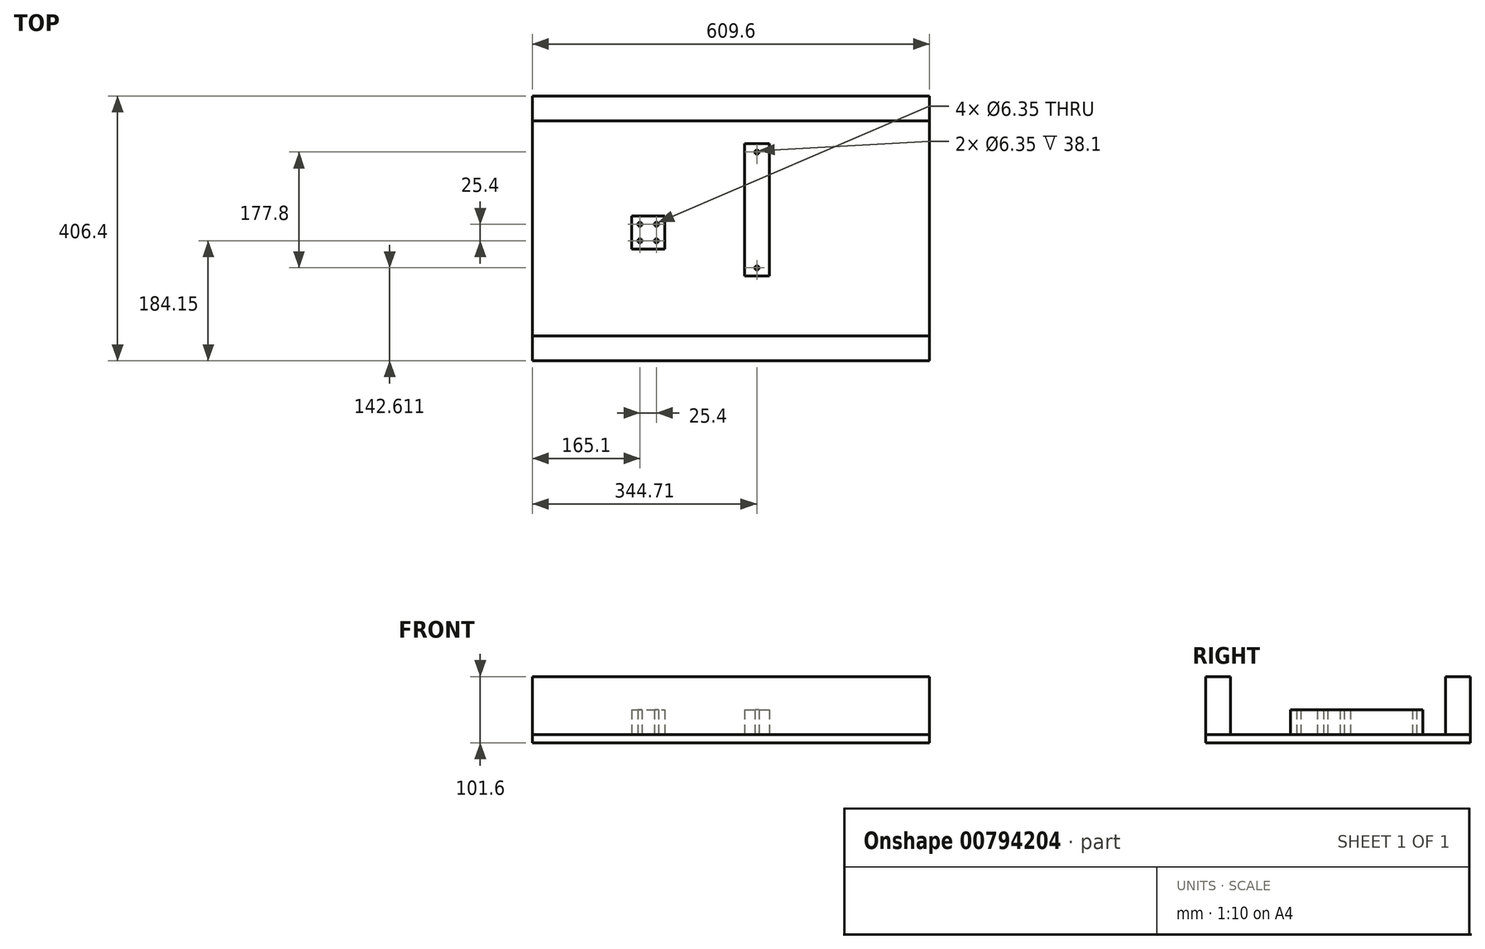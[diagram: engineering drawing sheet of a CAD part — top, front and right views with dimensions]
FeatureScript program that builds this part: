
annotation { "Feature Type Name" : "Feature", "Feature Type Description" : "" }
export const myFeature = defineFeature(function(context is Context, id is Id, definition is map)
    precondition{}
    {
        {
            var Q0;
            Q0=qCreatedBy(makeId("Top.planeOp"),FACE);
            var sketch = newSketch(context, id + "F0", { "sketchPlane" : qUnion([Q0])});
            skLineSegment(sketch, "E0.bottom", {"start": v(304.8, -203.2) * mm, "end": v(-304.8, -203.2) * mm});
            skLineSegment(sketch, "E0.top", {"start": v(304.8, 203.2) * mm, "end": v(-304.8, 203.2) * mm});
            skLineSegment(sketch, "E0.left", {"start": v(304.8, -203.2) * mm, "end": v(304.8, 203.2) * mm});
            skLineSegment(sketch, "E0.right", {"start": v(-304.8, -203.2) * mm, "end": v(-304.8, 203.2) * mm});
            skPoint(sketch, "E0.middle", {"position": v(0, 0) * mm});
            skSolve(sketch);
        }
        {
            var Q0;
            Q0=makeQuery(id+"F0.imprint","IMPRINT",FACE,{"disambiguationData":[TD([[makeQuery(id+"F0.imprint","IMPRINT",EDGE,{"derivedFrom":sQuery(id+"F0.wireOp",EDGE,"E0.bottom")}),-1.0]])]});
            extrude(context, id + "F1", {"entities" : qUnion([Q0]), "depth" : 12.7 * mm, "offsetDistance" : 25.4 * mm});
        }
        {
            var Q0;
            Q0=makeQuery(id+"F1.opExtrude","CAP_FACE",FACE,{"disambiguationData":[OSD([sQuery(id+"F0.wireOp",EDGE,"E0.bottom"),sQuery(id+"F0.wireOp",EDGE,"E0.top"),sQuery(id+"F0.wireOp",EDGE,"E0.left"),sQuery(id+"F0.wireOp",EDGE,"E0.right")])],"isStart":false});
            var sketch = newSketch(context, id + "F2", { "sketchPlane" : qUnion([Q0])});
            skLineSegment(sketch, "E1.bottom", {"start": v(-304.8, -203.2) * mm, "end": v(304.8, -203.2) * mm});
            skLineSegment(sketch, "E1.top", {"start": v(-304.8, -165.1) * mm, "end": v(304.8, -165.1) * mm});
            skLineSegment(sketch, "E1.left", {"start": v(-304.8, -203.2) * mm, "end": v(-304.8, -165.1) * mm});
            skLineSegment(sketch, "E1.right", {"start": v(304.8, -203.2) * mm, "end": v(304.8, -165.1) * mm});
            skLineSegment(sketch, "E2.bottom", {"start": v(-304.8, 203.2) * mm, "end": v(304.8, 203.2) * mm});
            skLineSegment(sketch, "E2.top", {"start": v(-304.8, 165.1) * mm, "end": v(304.8, 165.1) * mm});
            skLineSegment(sketch, "E2.left", {"start": v(-304.8, 203.2) * mm, "end": v(-304.8, 165.1) * mm});
            skLineSegment(sketch, "E2.right", {"start": v(304.8, 203.2) * mm, "end": v(304.8, 165.1) * mm});
            skSolve(sketch);
        }
        {
            var Q0;
            Q0=makeQuery(id+"F2.imprint","IMPRINT",FACE,{"disambiguationData":[TD([[makeQuery(id+"F2.imprint","IMPRINT",EDGE,{"derivedFrom":sQuery(id+"F2.wireOp",EDGE,"E2.bottom")}),1.0]])]});
            var Q1;
            Q1=makeQuery(id+"F2.imprint","IMPRINT",FACE,{"disambiguationData":[TD([[makeQuery(id+"F2.imprint","IMPRINT",EDGE,{"derivedFrom":sQuery(id+"F2.wireOp",EDGE,"E1.bottom")}),-1.0]])]});
            extrude(context, id + "F3", {"entities" : qUnion([Q0, Q1]), "depth" : 88.9 * mm, "offsetDistance" : 25.4 * mm});
        }
        {
            var Q0;
            Q0=makeQuery(id+"F1.opExtrude","CAP_FACE",FACE,{"disambiguationData":[OSD([sQuery(id+"F0.wireOp",EDGE,"E0.bottom"),sQuery(id+"F0.wireOp",EDGE,"E0.top"),sQuery(id+"F0.wireOp",EDGE,"E0.left"),sQuery(id+"F0.wireOp",EDGE,"E0.right")])],"isStart":false});
            var sketch = newSketch(context, id + "F4", { "sketchPlane" : qUnion([Q0])});
            skLineSegment(sketch, "E3.bottom", {"start": v(-152.4, 19.05) * mm, "end": v(-101.6, 19.05) * mm});
            skLineSegment(sketch, "E3.top", {"start": v(-152.4, -31.75) * mm, "end": v(-101.6, -31.75) * mm});
            skLineSegment(sketch, "E3.left", {"start": v(-152.4, 19.05) * mm, "end": v(-152.4, -31.75) * mm});
            skLineSegment(sketch, "E3.right", {"start": v(-101.6, 19.05) * mm, "end": v(-101.6, -31.75) * mm});
            skCircle(sketch, "E4", {"center": v(-139.7, 6.35) * mm, "radius": 3.18 * mm});
            skCircle(sketch, "E5.0.1.0", {"center": v(-139.7, -19.05) * mm, "radius": 3.18 * mm});
            skCircle(sketch, "E5.1.0.0", {"center": v(-114.3, 6.35) * mm, "radius": 3.18 * mm});
            skCircle(sketch, "E5.1.1.0", {"center": v(-114.3, -19.05) * mm, "radius": 3.18 * mm});
            skLineSegment(sketch, "E5.direction1", {"start": v(-139.7, 6.35) * mm, "end": v(-114.3, 6.35) * mm, "construction": true});
            skLineSegment(sketch, "E5.direction2", {"start": v(-139.7, 6.35) * mm, "end": v(-139.7, -19.05) * mm, "construction": true});
            skSolve(sketch);
        }
        {
            var Q0;
            Q0=makeQuery(id+"F4.imprint","IMPRINT",FACE,{"disambiguationData":[TD([[makeQuery(id+"F4.imprint","IMPRINT",EDGE,{"derivedFrom":sQuery(id+"F4.wireOp",EDGE,"E3.bottom")}),-1.0]])]});
            extrude(context, id + "F5", {"entities" : qUnion([Q0]), "depth" : 38.1 * mm, "offsetDistance" : 25.4 * mm});
        }
        {
            var Q0;
            Q0=makeQuery(id+"F1.opExtrude","CAP_FACE",FACE,{"disambiguationData":[OSD([sQuery(id+"F0.wireOp",EDGE,"E0.bottom"),sQuery(id+"F0.wireOp",EDGE,"E0.top"),sQuery(id+"F0.wireOp",EDGE,"E0.left"),sQuery(id+"F0.wireOp",EDGE,"E0.right")])],"isStart":false});
            var sketch = newSketch(context, id + "F6", { "sketchPlane" : qUnion([Q0])});
            skLineSegment(sketch, "E6.bottom", {"start": v(20.86, 129.91) * mm, "end": v(58.96, 129.91) * mm});
            skLineSegment(sketch, "E6.top", {"start": v(20.86, -73.29) * mm, "end": v(58.96, -73.29) * mm});
            skLineSegment(sketch, "E6.left", {"start": v(20.86, 129.91) * mm, "end": v(20.86, -73.29) * mm});
            skLineSegment(sketch, "E6.right", {"start": v(58.96, 129.91) * mm, "end": v(58.96, -73.29) * mm});
            skCircle(sketch, "E7", {"center": v(39.91, 117.21) * mm, "radius": 3.18 * mm});
            skPoint(sketch, "E7.centerSnap0", {"position": v(39.91, 129.91) * mm});
            skCircle(sketch, "E8.0.1.0", {"center": v(39.91, -60.59) * mm, "radius": 3.18 * mm});
            skLineSegment(sketch, "E8.direction1", {"start": v(39.91, 117.21) * mm, "end": v(65.31, 117.21) * mm, "construction": true});
            skLineSegment(sketch, "E8.direction2", {"start": v(39.91, 117.21) * mm, "end": v(39.91, -60.59) * mm, "construction": true});
            skSolve(sketch);
        }
        {
            var Q0;
            Q0=makeQuery(id+"F6.imprint","IMPRINT",FACE,{"disambiguationData":[TD([[makeQuery(id+"F6.imprint","IMPRINT",EDGE,{"derivedFrom":sQuery(id+"F6.wireOp",EDGE,"E6.bottom")}),-1.0]])]});
            extrude(context, id + "F7", {"entities" : qUnion([Q0]), "operationType" : NewBodyOperationType.ADD, "depth" : 38.1 * mm, "offsetDistance" : 25.4 * mm});
        }
    });
